SOLIDWORKS PART (.sldprt)
format: sldprt  version: not decoded by parser v0  size: 165,376 bytes
history: native  units: mm
features: sketch x8, extrude x4, fillet x4, plane x3, revolve x2, material x1, sweep x1 (+10 scaffold rows collapsed)
feature tree (33):
  scaffold x10  (default folders/planes/origin — collapsed)
  material  "Matériau <non spécifié>"
  plane  "Plan de face"
  plane  "Plan de dessus"
  plane  "Plan de droite"
  sketch  "Esquisse4"  dims[c1.D1=5.0mm c1.D2=590.5mm c1.D3=51.5mm c2.D2=~591.809052mm c2.D4=~596.809052mm]
  sketch  "Esquisse5"  dims[D1=10.0mm]
  sweep  "Balayage1"
  sketch  "Esquisse7"  dims[D1=10.0mm]
  extrude  "Extrusion1"  Depth=220mm
  sketch  "Esquisse8"
  revolve  "Révolution2"  Angle=90deg
  sketch  "Esquisse11"  dims[c1.D1=10.0mm c1.D2=10.0mm c1.D4=10.0mm c1.D3=57.5mm c2.D4=65.0mm]
  extrude  "Extrusion4"  Depth=40mm
  sketch  "Esquisse12"  dims[D1=5.0mm]
  extrude  "Extrusion5"  Depth=20mm
  fillet  "Congé2"  Radius=2mm
  fillet  "Congé6"  Radius=2.5mm
  fillet  "Congé7"  Radius=5mm
  fillet  "Congé9"  Radius=2mm
  sketch  "Esquisse15"  dims[D1=10.0mm]
  revolve  "Révolution5"  Angle=360deg
  sketch  "Esquisse14"  dims[D1=0.0mm]
  extrude  "Extrusion6"  Depth=2000mm
decode coverage: 17 of 19 modeling features carry decoded parameters
note: ~ marks probable driven/reference dimensions
note: suppression state not decoded; provenance and decode notes live in map.json
